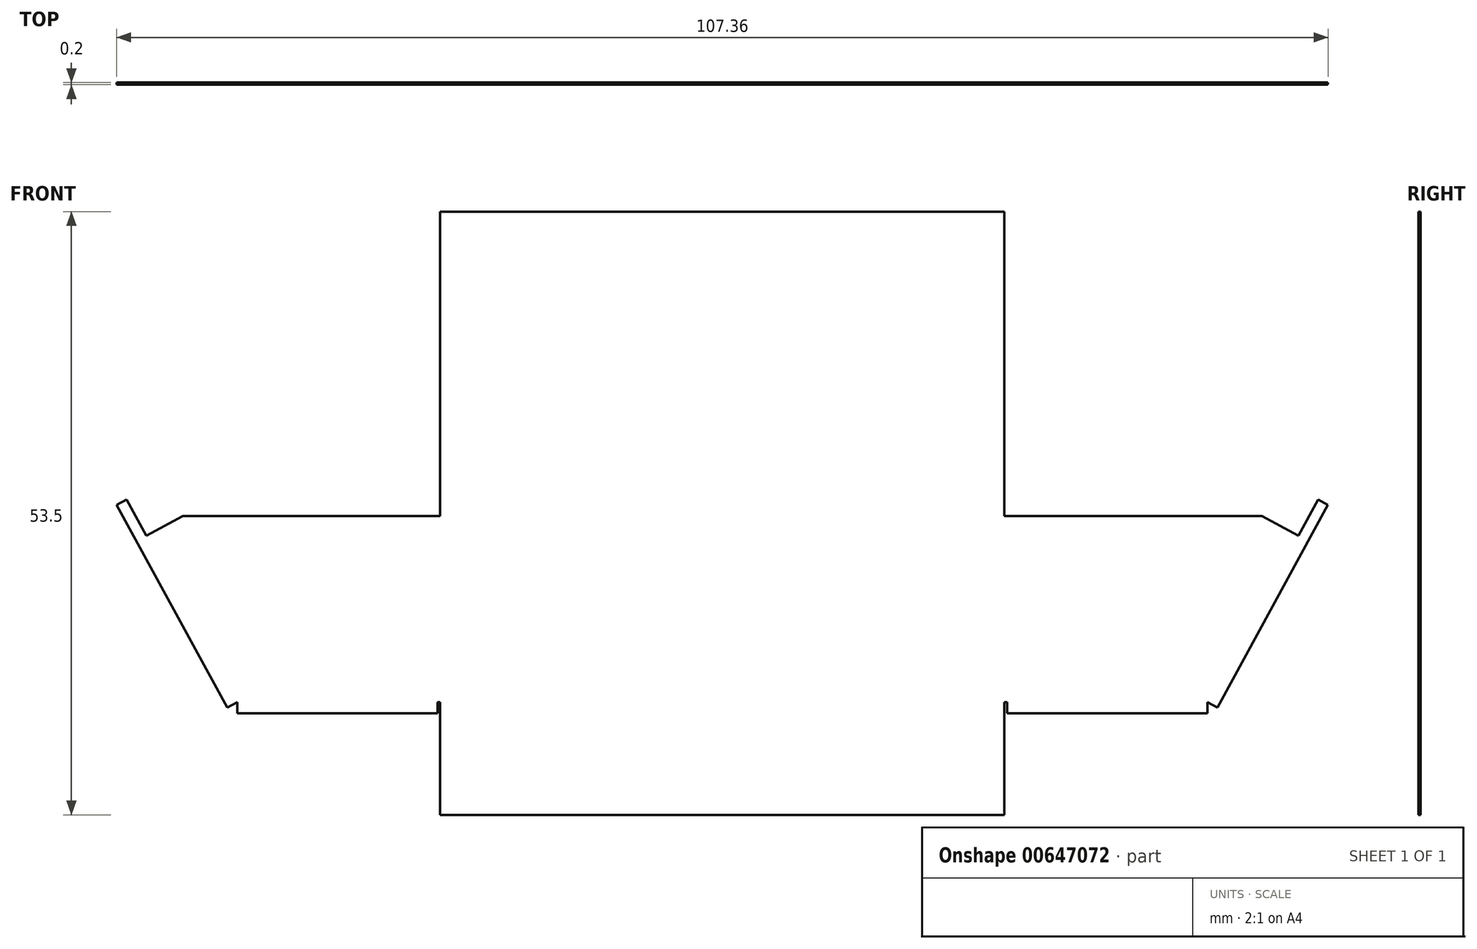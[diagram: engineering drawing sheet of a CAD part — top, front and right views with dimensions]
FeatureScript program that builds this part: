
annotation { "Feature Type Name" : "Feature", "Feature Type Description" : "" }
export const myFeature = defineFeature(function(context is Context, id is Id, definition is map)
    precondition{}
    {
        {
            var Q0;
            Q0=qCreatedBy(makeId("Front.planeOp"),FACE);
            var sketch = newSketch(context, id + "F0", { "sketchPlane" : qUnion([Q0])});
            skLineSegment(sketch, "E0.bottom", {"start": v(-25, 8.25) * mm, "end": v(25, 8.25) * mm});
            skLineSegment(sketch, "E0.top", {"start": v(-25, -8.25) * mm, "end": v(25, -8.25) * mm});
            skLineSegment(sketch, "E0.left", {"start": v(-25, 8.25) * mm, "end": v(-25, -8.25) * mm});
            skLineSegment(sketch, "E0.right", {"start": v(25, 8.25) * mm, "end": v(25, -8.25) * mm});
            skPoint(sketch, "E0.middle", {"position": v(0, 0) * mm});
            skLineSegment(sketch, "E1", {"start": v(-25, 8.25) * mm, "end": v(-47.82, 8.25) * mm});
            skLineSegment(sketch, "E2", {"start": v(-52, 8.25) * mm, "end": v(-43, -8.25) * mm});
            skLineSegment(sketch, "E3", {"start": v(-43, -8.25) * mm, "end": v(-25, -8.25) * mm});
            skLineSegment(sketch, "E4", {"start": v(43, -8.25) * mm, "end": v(25, -8.25) * mm});
            skLineSegment(sketch, "E5", {"start": v(25, 8.25) * mm, "end": v(25, 35.25) * mm});
            skLineSegment(sketch, "E6", {"start": v(25, 35.25) * mm, "end": v(-25, 35.25) * mm});
            skLineSegment(sketch, "E7", {"start": v(-25, 35.25) * mm, "end": v(-25, 8.25) * mm});
            skLineSegment(sketch, "E8", {"start": v(-25, -8.25) * mm, "end": v(-25, -18.25) * mm});
            skLineSegment(sketch, "E9", {"start": v(-25, -18.25) * mm, "end": v(25, -18.25) * mm});
            skLineSegment(sketch, "E10", {"start": v(25, -18.25) * mm, "end": v(25, -8.25) * mm});
            skLineSegment(sketch, "E11", {"start": v(25, 8.25) * mm, "end": v(47.82, 8.25) * mm});
            skLineSegment(sketch, "E12", {"start": v(52, 8.25) * mm, "end": v(43, -8.25) * mm});
            skLineSegment(sketch, "E13", {"start": v(43, -8.25) * mm, "end": v(43.88, -8.73) * mm});
            skLineSegment(sketch, "E14", {"start": v(52.88, 7.77) * mm, "end": v(43.88, -8.73) * mm});
            skLineSegment(sketch, "E15", {"start": v(-43, -8.25) * mm, "end": v(-43.88, -8.73) * mm});
            skLineSegment(sketch, "E16", {"start": v(-43.88, -8.73) * mm, "end": v(-52.88, 7.77) * mm});
            skLineSegment(sketch, "E17.0", {"start": v(43, -9.25) * mm, "end": v(25.25, -9.25) * mm});
            skLineSegment(sketch, "E18.0", {"start": v(-43, -9.25) * mm, "end": v(-25.25, -9.25) * mm});
            skLineSegment(sketch, "E19", {"start": v(-43, -9.25) * mm, "end": v(-43, -8.25) * mm});
            skLineSegment(sketch, "E20", {"start": v(43, -9.25) * mm, "end": v(43, -8.25) * mm});
            skLineSegment(sketch, "E21.0", {"start": v(25.25, -9.25) * mm, "end": v(25.25, -8.25) * mm});
            skLineSegment(sketch, "E22.0", {"start": v(-25.25, -8.25) * mm, "end": v(-25.25, -9.25) * mm});
            skLineSegment(sketch, "E23.0", {"start": v(-47.82, 8.25) * mm, "end": v(-51.04, 6.5) * mm});
            skLineSegment(sketch, "E24.0", {"start": v(47.82, 8.25) * mm, "end": v(51.04, 6.5) * mm});
            skLineSegment(sketch, "E25", {"start": v(52, 8.25) * mm, "end": v(52.8, 9.71) * mm});
            skLineSegment(sketch, "E26", {"start": v(52.8, 9.71) * mm, "end": v(53.68, 9.23) * mm});
            skLineSegment(sketch, "E27", {"start": v(53.68, 9.23) * mm, "end": v(52.88, 7.77) * mm});
            skLineSegment(sketch, "E28", {"start": v(-52.88, 7.77) * mm, "end": v(-53.68, 9.23) * mm});
            skLineSegment(sketch, "E29", {"start": v(-53.68, 9.23) * mm, "end": v(-52.8, 9.7) * mm});
            skLineSegment(sketch, "E30", {"start": v(-52.8, 9.7) * mm, "end": v(-52, 8.25) * mm});
            skSolve(sketch);
        }
        {
            var Q0;
            Q0 = qSketchRegion(id + "F0", true);
            extrude(context, id + "F1", {"entities" : qUnion([Q0]), "depth" : .2 * mm, "offsetDistance" : 25 * mm});
        }
    });
